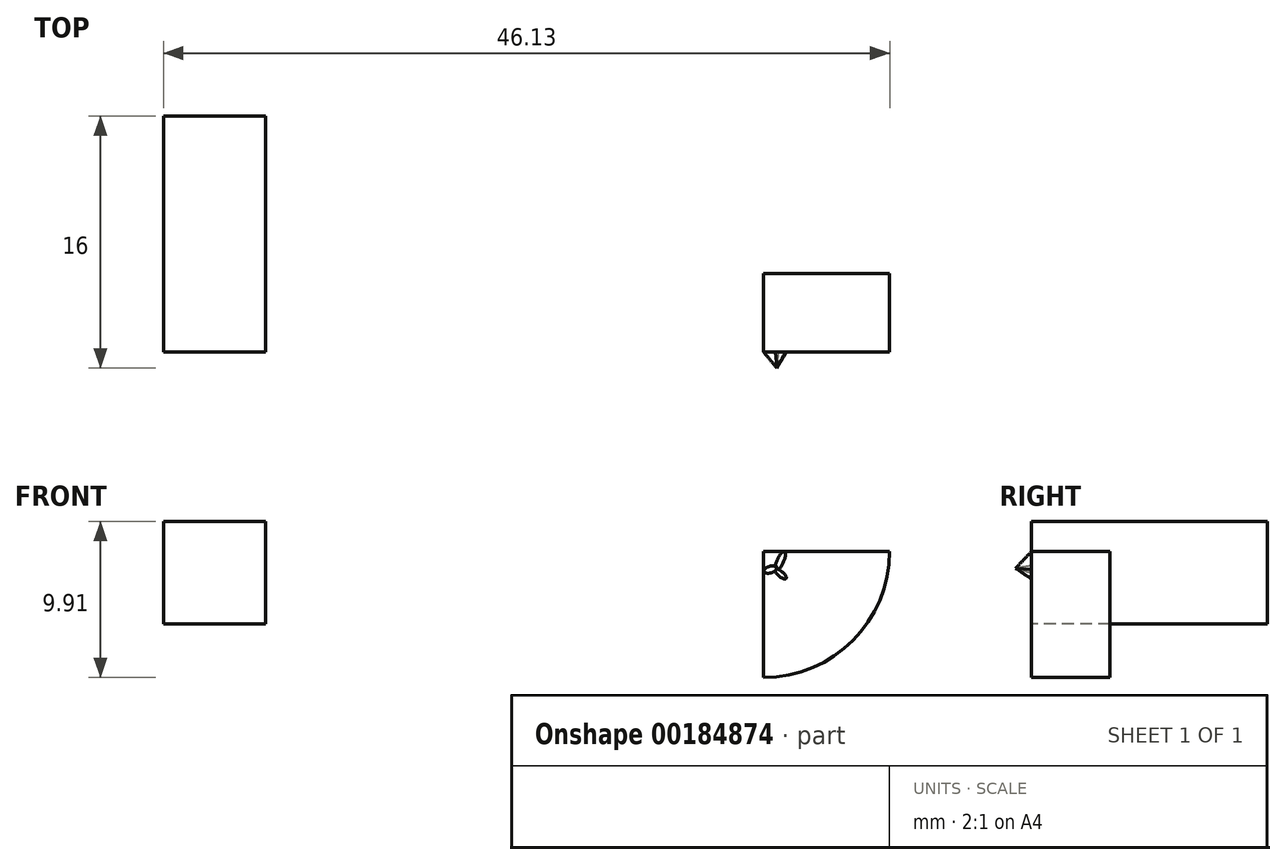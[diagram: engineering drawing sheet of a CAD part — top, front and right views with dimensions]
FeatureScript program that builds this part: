
annotation { "Feature Type Name" : "Feature", "Feature Type Description" : "" }
export const myFeature = defineFeature(function(context is Context, id is Id, definition is map)
    precondition{}
    {
        {
            var Q0;
            Q0=qCreatedBy(makeId("Front.planeOp"),FACE);
            var sketch = newSketch(context, id + "F0", { "sketchPlane" : qUnion([Q0])});
            skLineSegment(sketch, "E0.bottom", {"start": v(-32.22, 30.9) * mm, "end": v(-25.71, 30.9) * mm});
            skLineSegment(sketch, "E0.top", {"start": v(-32.22, 24.39) * mm, "end": v(-25.71, 24.39) * mm});
            skLineSegment(sketch, "E0.left", {"start": v(-32.22, 30.9) * mm, "end": v(-32.22, 24.39) * mm});
            skLineSegment(sketch, "E0.right", {"start": v(-25.71, 30.9) * mm, "end": v(-25.71, 24.39) * mm});
            skArc(sketch, "E1", {"start": v(5.9, 20.98) * mm, "mid": v(11.56, 23.33) * mm, "end": v(13.9, 28.98) * mm});
            skLineSegment(sketch, "E2", {"start": v(5.9, 28.98) * mm, "end": v(5.9, 20.98) * mm});
            skLineSegment(sketch, "E3", {"start": v(5.9, 28.98) * mm, "end": v(13.9, 28.98) * mm});
            skSolve(sketch);
        }
        {
            var Q0;
            Q0=makeQuery(id+"F0.imprint","IMPRINT",FACE,{"disambiguationData":[TD([[makeQuery(id+"F0.imprint","IMPRINT",EDGE,{"derivedFrom":sQuery(id+"F0.wireOp",EDGE,"E0.bottom")}),-1.0]])]});
            extrude(context, id + "F1", {"entities" : qUnion([Q0]), "oppositeDirection" : true, "depth" : 10 * mm});
        }
        {
            var Q0;
            Q0 = qSketchRegion(id + "F0", true);
            extrude(context, id + "F2", {"entities" : qUnion([Q0]), "operationType" : NewBodyOperationType.ADD, "depth" : 5 * mm});
        }
        {
            var Q0;
            Q0=qCreatedBy(makeId("Front.planeOp"),FACE);
            cPlane(context, id + "F3", {"entities" : qUnion([Q0]), "cplaneType" : CPlaneType.OFFSET, "offset" : 5 * mm, "width" : 150 * mm, "height" : 150 * mm});
        }
        {
            var Q0;
            Q0=makeQuery(id+"F2.opExtrude","CAP_FACE",FACE,{"disambiguationData":[OSD([sQuery(id+"F0.wireOp",EDGE,"E1"),sQuery(id+"F0.wireOp",EDGE,"E2"),sQuery(id+"F0.wireOp",EDGE,"E3")])],"isStart":true});
            cPlane(context, id + "F4", {"entities" : qUnion([Q0]), "cplaneType" : CPlaneType.OFFSET, "offset" : 6 * mm, "oppositeDirection" : true, "width" : 150 * mm, "height" : 150 * mm});
        }
        {
            var Q0;
            Q0=makeQuery(id+"F2.opExtrude","CAP_FACE",FACE,{"disambiguationData":[OSD([sQuery(id+"F0.wireOp",EDGE,"E1"),sQuery(id+"F0.wireOp",EDGE,"E2"),sQuery(id+"F0.wireOp",EDGE,"E3")])],"isStart":false});
            var sketch = newSketch(context, id + "F5", { "sketchPlane" : qUnion([Q0])});
            skLineSegment(sketch, "E4.bottom", {"start": v(-45.84, 32.02) * mm, "end": v(-35.5, 32.02) * mm});
            skLineSegment(sketch, "E4.top", {"start": v(-45.84, 21.67) * mm, "end": v(-35.5, 21.67) * mm});
            skLineSegment(sketch, "E4.left", {"start": v(-45.84, 32.02) * mm, "end": v(-45.84, 21.67) * mm});
            skLineSegment(sketch, "E4.right", {"start": v(-35.5, 32.02) * mm, "end": v(-35.5, 21.67) * mm});
            skSolve(sketch);
        }
        {
            var Q0;
            Q0=makeQuery(id+"F5.imprint","IMPRINT",FACE,{"disambiguationData":[TD([[makeQuery(id+"F5.imprint","IMPRINT",EDGE,{"derivedFrom":makeQuery(id+"F2.opExtrude","CAP_EDGE",EDGE,{"disambiguationData":[OSD([sQuery(id+"F0.wireOp",EDGE,"E1")])],"isStart":false})}),1.0]])]});
            var sketch = newSketch(context, id + "F6", { "sketchPlane" : qUnion([Q0])});
            skEllipticalArc(sketch, "E5.trimOffspring", {});
            skEllipticalArc(sketch, "E6", {});
            skEllipticalArc(sketch, "E7", {});
            skEllipticalArc(sketch, "E8", {});
            skEllipticalArc(sketch, "E9", {});
            const initialGuessF6  = {"E5.trimOffspring": [0.0069868820719406165, 0.0275468658655913, -0.7703945328743967, 0.6375674581699102, 0.000446961243664411, 0.0001642768742522988, 0.47747101922247925, 5.423848400941894], "E6": [0.006963134743271895, 0.02837802283466183, 0.40285632341449307, 0.9152632313629583, 0.0006478875058329403, 0.00020951479278244782, 3.69335296094582, 2.275599678531766], "E7": [0.006339353043586055, 0.027837028726935564, -0.9597407574642836, -0.2808873056261734, 0.00044218600360457466, 0.00021416766607753042, 3.7677822988535015, 2.1854106589734803], "E8": [0.00779321976006031, 0.028022604063153267, 1, 0, 0.0005133077502250671, 0.0002114917042019627, 1.2904202335894923, 1.0822592253579189], "E9": [0.008159867487847805, 0.028560353443026543, 0.4688219182387807, 0.8832927085507443, 0.00044486651159702937, 9.576178302389002e-05, 3.7343209763264125, 2.6926140824731672]};
            skSetInitialGuess(sketch, initialGuessF6);
            skSolve(sketch);
        }
        {
            var Q0;
            Q0=qCreatedBy(id+"F4.planeOp",FACE);
            var sketch = newSketch(context, id + "F7", { "sketchPlane" : qUnion([Q0])});
            skPoint(sketch, "E10", {"position": v(-6.74, 27.92) * mm});
            skPoint(sketch, "E11", {"position": v(-8, 28.2) * mm});
            skSolve(sketch);
        }
        {
            var Q1;
            {var subQ1=sQuery(id+"F6.wireOp",EDGE,"E6");var subQ5=sQuery(id+"F6.wireOp",EDGE,"E5.trimOffspring");var subQ6=makeQuery(id+"F6.imprint","INTERSECT",VERTEX,{"derivedFrom":[subQ5,subQ1]});Q1=makeQuery(id+"F6.imprint","IMPRINT",FACE,{"disambiguationData":[TD([[makeQuery(id+"F6.imprint","IMPRINT",EDGE,{"disambiguationData":[TD([[subQ6,1.0]])],"derivedFrom":subQ5}),1.0]])]});}
            var Q2;
            Q2=sQuery(id+"F7.wireOp",VERTEX,"E10");
            loft(context, id + "F8", {"operationType" : NewBodyOperationType.ADD, "sheetProfilesArray" : [{ "sheetProfileEntities" : qUnion([Q1]) }, { "sheetProfileEntities" : qUnion([Q2]) }]});
        }
    });
